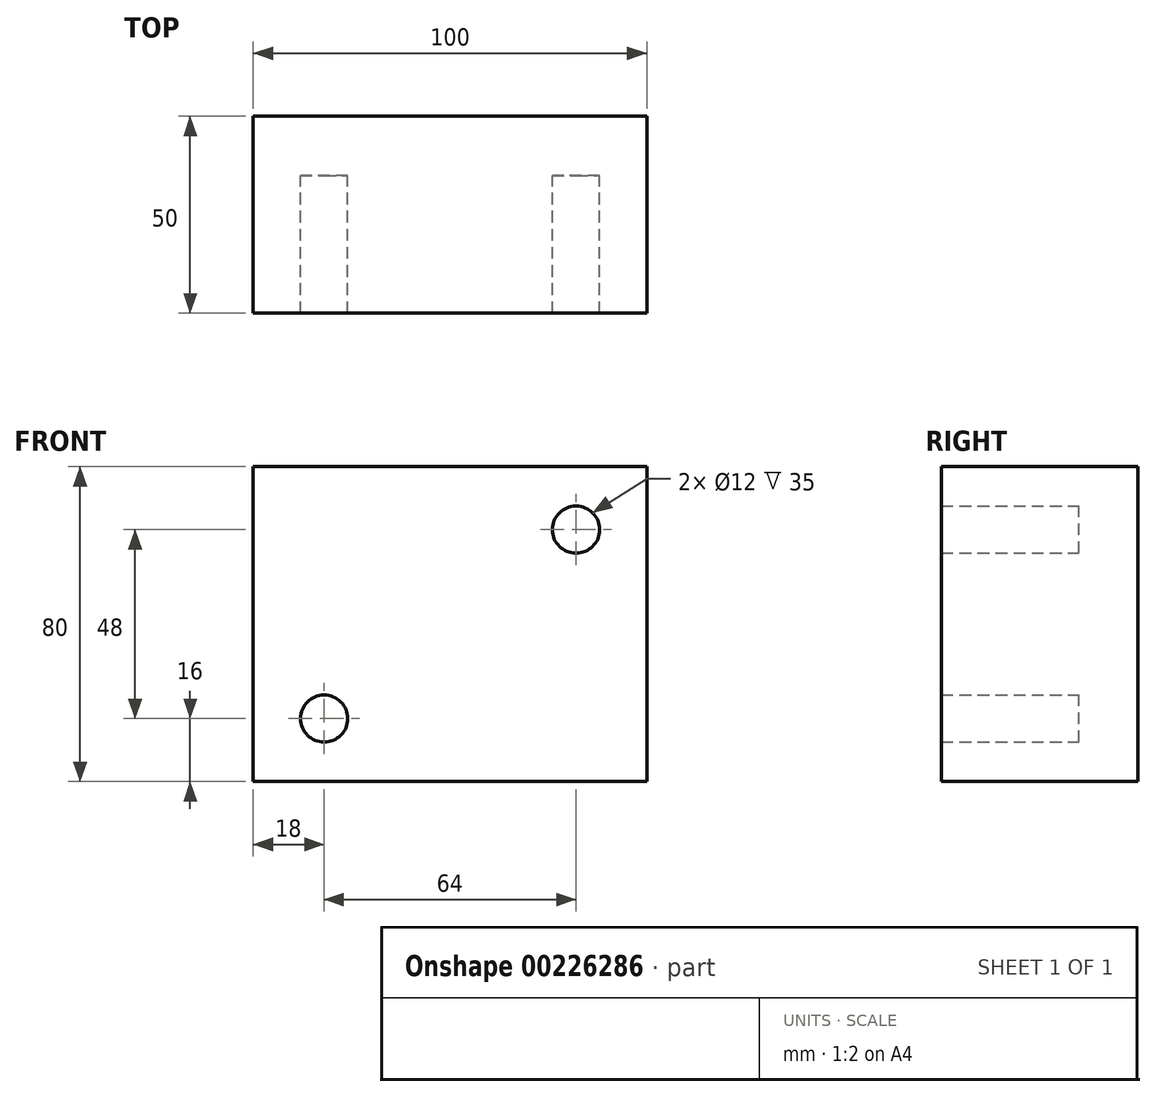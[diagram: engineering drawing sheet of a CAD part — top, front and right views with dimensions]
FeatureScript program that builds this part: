
annotation { "Feature Type Name" : "Feature", "Feature Type Description" : "" }
export const myFeature = defineFeature(function(context is Context, id is Id, definition is map)
    precondition{}
    {
        {
            var Q0;
            Q0=qCreatedBy(makeId("Front.planeOp"),FACE);
            var sketch = newSketch(context, id + "F0", { "sketchPlane" : qUnion([Q0])});
            skLineSegment(sketch, "E0.bottom", {"start": v(-50, 40) * mm, "end": v(50, 40) * mm});
            skLineSegment(sketch, "E0.top", {"start": v(-50, -40) * mm, "end": v(50, -40) * mm});
            skLineSegment(sketch, "E0.left", {"start": v(-50, 40) * mm, "end": v(-50, -40) * mm});
            skLineSegment(sketch, "E0.right", {"start": v(50, 40) * mm, "end": v(50, -40) * mm});
            skSolve(sketch);
        }
        {
            var Q0;
            Q0=makeQuery(id+"F0.imprint","IMPRINT",FACE,{"disambiguationData":[TD([[makeQuery(id+"F0.imprint","IMPRINT",EDGE,{"derivedFrom":sQuery(id+"F0.wireOp",EDGE,"E0.bottom")}),-1.0]])]});
            extrude(context, id + "F1", {"entities" : qUnion([Q0]), "depth" : 15 * mm});
        }
        {
            var Q0;
            Q0=makeQuery(id+"F1.opExtrude","CAP_FACE",FACE,{"disambiguationData":[OSD([sQuery(id+"F0.wireOp",EDGE,"E0.bottom"),sQuery(id+"F0.wireOp",EDGE,"E0.top"),sQuery(id+"F0.wireOp",EDGE,"E0.left"),sQuery(id+"F0.wireOp",EDGE,"E0.right")])],"isStart":false});
            var sketch = newSketch(context, id + "F2", { "sketchPlane" : qUnion([Q0])});
            skCircle(sketch, "E1", {"center": v(-32, 24) * mm, "radius": 6 * mm});
            skCircle(sketch, "E2.MirrorC", {"center": v(32, 24) * mm, "radius": 6 * mm});
            skCircle(sketch, "E3.MirrorC", {"center": v(32, -24) * mm, "radius": 6 * mm});
            skCircle(sketch, "E4.MirrorC", {"center": v(-32, -24) * mm, "radius": 6 * mm});
            skSolve(sketch);
        }
        {
            var Q0;
            Q0=makeQuery(id+"F2.imprint","IMPRINT",FACE,{"disambiguationData":[TD([[makeQuery(id+"F2.imprint","IMPRINT",EDGE,{"derivedFrom":sQuery(id+"F2.wireOp",EDGE,"E4.MirrorC")}),-1.0]])]});
            var Q1;
            Q1=makeQuery(id+"F2.imprint","IMPRINT",FACE,{"disambiguationData":[TD([[makeQuery(id+"F2.imprint","IMPRINT",EDGE,{"derivedFrom":sQuery(id+"F2.wireOp",EDGE,"E1")}),1.0]])]});
            var Q2;
            Q2=makeQuery(id+"F2.imprint","IMPRINT",FACE,{"disambiguationData":[TD([[makeQuery(id+"F2.imprint","IMPRINT",EDGE,{"derivedFrom":sQuery(id+"F2.wireOp",EDGE,"E2.MirrorC")}),-1.0]])]});
            var Q3;
            Q3=makeQuery(id+"F2.imprint","IMPRINT",FACE,{"disambiguationData":[TD([[makeQuery(id+"F2.imprint","IMPRINT",EDGE,{"derivedFrom":sQuery(id+"F2.wireOp",EDGE,"E3.MirrorC")}),1.0]])]});
            extrude(context, id + "F3", {"entities" : qUnion([Q0, Q1, Q2, Q3]), "operationType" : NewBodyOperationType.ADD, "depth" : 35 * mm});
        }
    });
